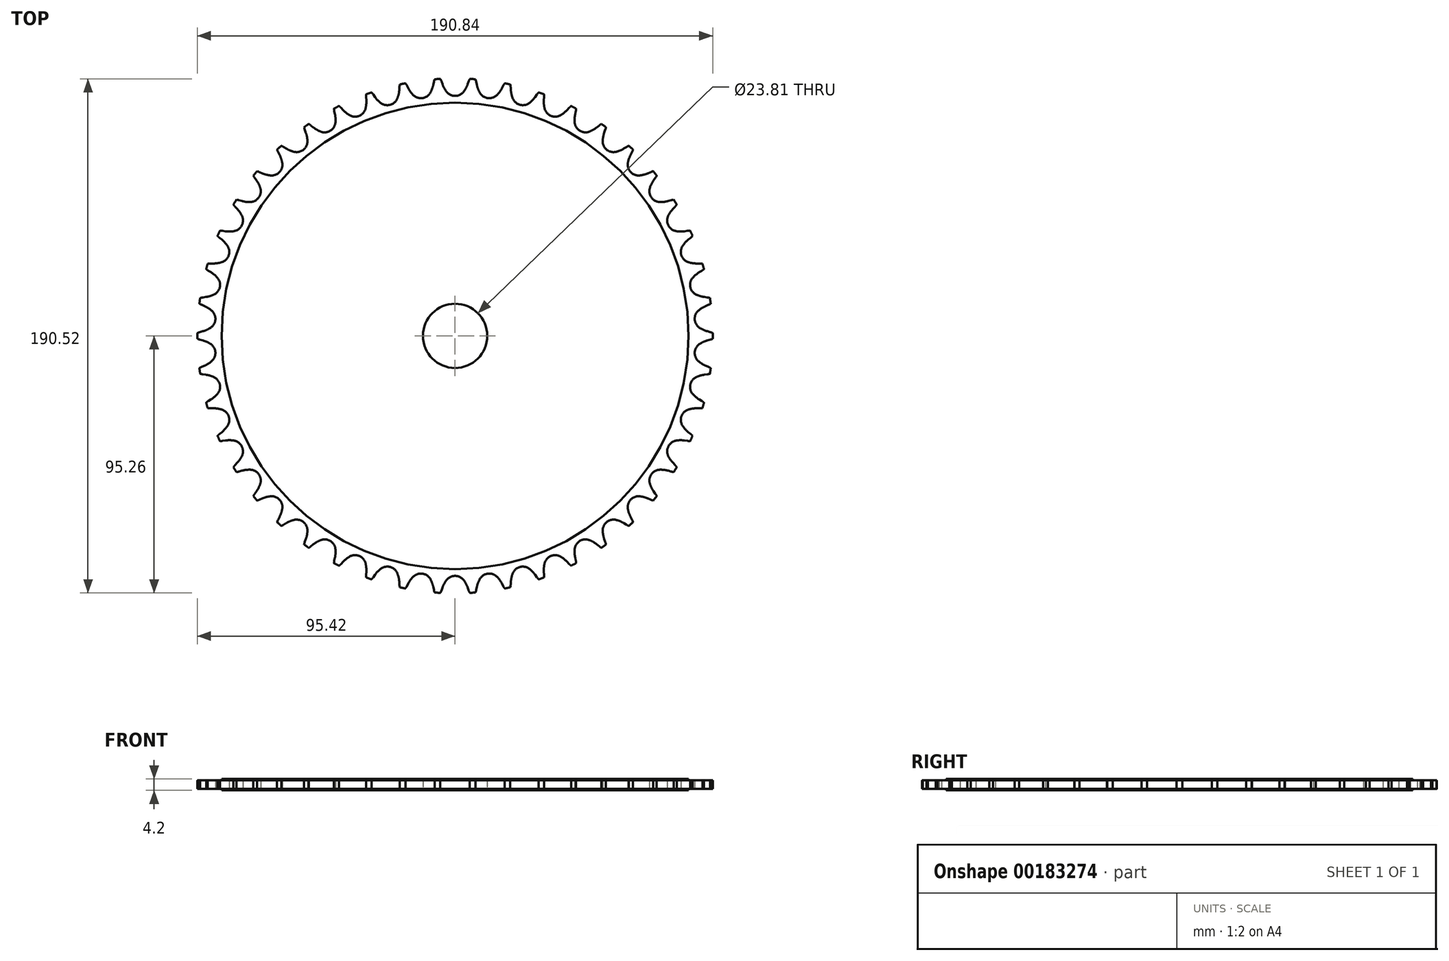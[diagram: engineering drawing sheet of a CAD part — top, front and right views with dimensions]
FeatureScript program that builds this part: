
annotation { "Feature Type Name" : "Feature", "Feature Type Description" : "" }
export const myFeature = defineFeature(function(context is Context, id is Id, definition is map)
    precondition{}
    {
        {
            var Q0;
            Q0=qCreatedBy(makeId("Top.planeOp"),FACE);
            var sketch = newSketch(context, id + "F0", { "sketchPlane" : qUnion([Q0])});
            skCircle(sketch, "E0", {"center": v(0, 0) * mm, "radius": 92.98 * mm, "construction": true});
            skArc(sketch, "E1", {"start": v(-3.24, 90.6) * mm, "mid": v(-1.81, 89.4) * mm, "end": v(0, 88.96) * mm});
            skArc(sketch, "E2", {"start": v(-4.67, 93.27) * mm, "mid": v(-4.05, 91.88) * mm, "end": v(-3.24, 90.6) * mm});
            skLineSegment(sketch, "E3", {"start": v(-4.67, 93.27) * mm, "end": v(-5.06, 94.36) * mm});
            skArc(sketch, "E4", {"start": v(-5.06, 94.36) * mm, "mid": v(-5.7, 95.68) * mm, "end": v(-6.62, 96.8) * mm});
            skArc(sketch, "E5.MirrorCS", {"start": v(3.24, 90.6) * mm, "mid": v(1.81, 89.4) * mm, "end": v(0, 88.96) * mm});
            skArc(sketch, "E6.MirrorCS", {"start": v(4.67, 93.27) * mm, "mid": v(4.05, 91.88) * mm, "end": v(3.24, 90.6) * mm});
            skLineSegment(sketch, "E7.MirrorCS", {"start": v(4.67, 93.27) * mm, "end": v(5.06, 94.36) * mm});
            skArc(sketch, "E8.MirrorCS", {"start": v(5.06, 94.36) * mm, "mid": v(5.7, 95.68) * mm, "end": v(6.62, 96.8) * mm});
            skArc(sketch, "E9.1.0", {"start": v(-17.86, 92.8) * mm, "mid": v(-18.67, 94) * mm, "end": v(-19.74, 95) * mm});
            skArc(sketch, "E9.1.1", {"start": v(-7.84, 94.17) * mm, "mid": v(-7.38, 95.56) * mm, "end": v(-6.62, 96.8) * mm});
            skArc(sketch, "E9.1.2", {"start": v(-9.13, 90.2) * mm, "mid": v(-10.38, 88.81) * mm, "end": v(-12.11, 88.13) * mm});
            skArc(sketch, "E9.1.3", {"start": v(-17.33, 91.77) * mm, "mid": v(-16.52, 90.48) * mm, "end": v(-15.54, 89.32) * mm});
            skArc(sketch, "E9.1.4", {"start": v(-15.54, 89.32) * mm, "mid": v(-13.97, 88.32) * mm, "end": v(-12.11, 88.13) * mm});
            skArc(sketch, "E9.1.5", {"start": v(-8.07, 93.04) * mm, "mid": v(-8.5, 91.58) * mm, "end": v(-9.13, 90.2) * mm});
            skLineSegment(sketch, "E9.1.6", {"start": v(-8.07, 93.04) * mm, "end": v(-7.84, 94.17) * mm});
            skLineSegment(sketch, "E9.1.7", {"start": v(-17.33, 91.77) * mm, "end": v(-17.86, 92.8) * mm});
            skArc(sketch, "E9.2.0", {"start": v(-30.33, 89.5) * mm, "mid": v(-31.3, 90.59) * mm, "end": v(-32.5, 91.43) * mm});
            skArc(sketch, "E9.2.1", {"start": v(-20.59, 92.23) * mm, "mid": v(-20.32, 93.67) * mm, "end": v(-19.74, 95) * mm});
            skArc(sketch, "E9.2.2", {"start": v(-21.33, 88.11) * mm, "mid": v(-22.37, 86.57) * mm, "end": v(-24, 85.66) * mm});
            skArc(sketch, "E9.2.3", {"start": v(-29.66, 88.55) * mm, "mid": v(-28.7, 87.38) * mm, "end": v(-27.56, 86.37) * mm});
            skArc(sketch, "E9.2.4", {"start": v(-27.56, 86.37) * mm, "mid": v(-25.86, 85.6) * mm, "end": v(-24, 85.66) * mm});
            skArc(sketch, "E9.2.5", {"start": v(-20.67, 91.07) * mm, "mid": v(-20.89, 89.57) * mm, "end": v(-21.33, 88.11) * mm});
            skLineSegment(sketch, "E9.2.6", {"start": v(-20.67, 91.07) * mm, "end": v(-20.59, 92.23) * mm});
            skLineSegment(sketch, "E9.2.7", {"start": v(-29.66, 88.55) * mm, "end": v(-30.33, 89.5) * mm});
            skArc(sketch, "E9.3.0", {"start": v(-42.23, 84.54) * mm, "mid": v(-43.34, 85.48) * mm, "end": v(-44.64, 86.16) * mm});
            skArc(sketch, "E9.3.1", {"start": v(-32.96, 88.57) * mm, "mid": v(-32.89, 90.03) * mm, "end": v(-32.5, 91.43) * mm});
            skArc(sketch, "E9.3.2", {"start": v(-33.13, 84.39) * mm, "mid": v(-33.95, 82.72) * mm, "end": v(-35.44, 81.6) * mm});
            skArc(sketch, "E9.3.3", {"start": v(-41.44, 83.69) * mm, "mid": v(-40.32, 82.66) * mm, "end": v(-39.06, 81.81) * mm});
            skArc(sketch, "E9.3.4", {"start": v(-39.06, 81.81) * mm, "mid": v(-37.28, 81.27) * mm, "end": v(-35.44, 81.6) * mm});
            skArc(sketch, "E9.3.5", {"start": v(-32.88, 87.4) * mm, "mid": v(-32.9, 85.9) * mm, "end": v(-33.13, 84.39) * mm});
            skLineSegment(sketch, "E9.3.6", {"start": v(-32.88, 87.4) * mm, "end": v(-32.96, 88.57) * mm});
            skLineSegment(sketch, "E9.3.7", {"start": v(-41.44, 83.69) * mm, "end": v(-42.23, 84.54) * mm});
            skArc(sketch, "E9.4.0", {"start": v(-53.35, 78) * mm, "mid": v(-54.58, 78.79) * mm, "end": v(-55.96, 79.27) * mm});
            skArc(sketch, "E9.4.1", {"start": v(-44.7, 83.25) * mm, "mid": v(-44.84, 84.7) * mm, "end": v(-44.64, 86.16) * mm});
            skArc(sketch, "E9.4.2", {"start": v(-44.31, 79.1) * mm, "mid": v(-44.9, 77.32) * mm, "end": v(-46.22, 76.01) * mm});
            skArc(sketch, "E9.4.3", {"start": v(-52.45, 77.27) * mm, "mid": v(-51.2, 76.4) * mm, "end": v(-49.84, 75.73) * mm});
            skArc(sketch, "E9.4.4", {"start": v(-49.84, 75.73) * mm, "mid": v(-48, 75.44) * mm, "end": v(-46.22, 76.01) * mm});
            skArc(sketch, "E9.4.5", {"start": v(-44.47, 82.12) * mm, "mid": v(-44.28, 80.61) * mm, "end": v(-44.31, 79.1) * mm});
            skLineSegment(sketch, "E9.4.6", {"start": v(-44.47, 82.12) * mm, "end": v(-44.7, 83.25) * mm});
            skLineSegment(sketch, "E9.4.7", {"start": v(-52.45, 77.27) * mm, "end": v(-53.35, 78) * mm});
            skArc(sketch, "E9.5.0", {"start": v(-63.47, 70) * mm, "mid": v(-64.8, 70.62) * mm, "end": v(-66.23, 70.92) * mm});
            skArc(sketch, "E9.5.1", {"start": v(-55.63, 76.39) * mm, "mid": v(-55.96, 77.81) * mm, "end": v(-55.96, 79.27) * mm});
            skArc(sketch, "E9.5.2", {"start": v(-54.67, 72.32) * mm, "mid": v(-55.01, 70.49) * mm, "end": v(-56.14, 69) * mm});
            skArc(sketch, "E9.5.3", {"start": v(-62.48, 69.4) * mm, "mid": v(-61.13, 68.72) * mm, "end": v(-59.69, 68.24) * mm});
            skArc(sketch, "E9.5.4", {"start": v(-59.69, 68.24) * mm, "mid": v(-57.82, 68.2) * mm, "end": v(-56.14, 69) * mm});
            skArc(sketch, "E9.5.5", {"start": v(-55.24, 75.3) * mm, "mid": v(-54.84, 73.83) * mm, "end": v(-54.67, 72.32) * mm});
            skLineSegment(sketch, "E9.5.6", {"start": v(-55.24, 75.3) * mm, "end": v(-55.63, 76.39) * mm});
            skLineSegment(sketch, "E9.5.7", {"start": v(-62.48, 69.4) * mm, "end": v(-63.47, 70) * mm});
            skArc(sketch, "E9.6.0", {"start": v(-72.42, 60.71) * mm, "mid": v(-73.81, 61.14) * mm, "end": v(-75.27, 61.24) * mm});
            skArc(sketch, "E9.6.1", {"start": v(-65.51, 68.1) * mm, "mid": v(-66.03, 69.47) * mm, "end": v(-66.23, 70.92) * mm});
            skArc(sketch, "E9.6.2", {"start": v(-64, 64.2) * mm, "mid": v(-64.1, 62.34) * mm, "end": v(-65.02, 60.72) * mm});
            skArc(sketch, "E9.6.3", {"start": v(-71.35, 60.25) * mm, "mid": v(-69.92, 59.75) * mm, "end": v(-68.42, 59.48) * mm});
            skArc(sketch, "E9.6.4", {"start": v(-68.42, 59.48) * mm, "mid": v(-66.57, 59.7) * mm, "end": v(-65.02, 60.72) * mm});
            skArc(sketch, "E9.6.5", {"start": v(-64.98, 67.08) * mm, "mid": v(-64.39, 65.68) * mm, "end": v(-64, 64.2) * mm});
            skLineSegment(sketch, "E9.6.6", {"start": v(-64.98, 67.08) * mm, "end": v(-65.51, 68.1) * mm});
            skLineSegment(sketch, "E9.6.7", {"start": v(-71.35, 60.25) * mm, "end": v(-72.42, 60.71) * mm});
            skArc(sketch, "E9.7.0", {"start": v(-80, 50.29) * mm, "mid": v(-81.45, 50.52) * mm, "end": v(-82.9, 50.42) * mm});
            skArc(sketch, "E9.7.1", {"start": v(-74.18, 58.55) * mm, "mid": v(-74.88, 59.83) * mm, "end": v(-75.27, 61.24) * mm});
            skArc(sketch, "E9.7.2", {"start": v(-72.15, 54.9) * mm, "mid": v(-71.99, 53.03) * mm, "end": v(-72.68, 51.3) * mm});
            skArc(sketch, "E9.7.3", {"start": v(-78.9, 49.97) * mm, "mid": v(-77.4, 49.68) * mm, "end": v(-75.88, 49.6) * mm});
            skArc(sketch, "E9.7.4", {"start": v(-75.88, 49.6) * mm, "mid": v(-74.08, 50.07) * mm, "end": v(-72.68, 51.3) * mm});
            skArc(sketch, "E9.7.5", {"start": v(-73.5, 57.6) * mm, "mid": v(-72.73, 56.3) * mm, "end": v(-72.15, 54.9) * mm});
            skLineSegment(sketch, "E9.7.6", {"start": v(-73.5, 57.6) * mm, "end": v(-74.18, 58.55) * mm});
            skLineSegment(sketch, "E9.7.7", {"start": v(-78.9, 49.97) * mm, "end": v(-80, 50.29) * mm});
            skArc(sketch, "E9.8.0", {"start": v(-86.1, 38.92) * mm, "mid": v(-87.57, 38.96) * mm, "end": v(-89, 38.66) * mm});
            skArc(sketch, "E9.8.1", {"start": v(-81.46, 47.9) * mm, "mid": v(-82.33, 49.08) * mm, "end": v(-82.9, 50.42) * mm});
            skArc(sketch, "E9.8.2", {"start": v(-78.95, 44.56) * mm, "mid": v(-78.54, 42.74) * mm, "end": v(-78.99, 40.93) * mm});
            skArc(sketch, "E9.8.3", {"start": v(-84.96, 38.76) * mm, "mid": v(-83.45, 38.68) * mm, "end": v(-81.93, 38.8) * mm});
            skArc(sketch, "E9.8.4", {"start": v(-81.93, 38.8) * mm, "mid": v(-80.2, 39.52) * mm, "end": v(-78.99, 40.93) * mm});
            skArc(sketch, "E9.8.5", {"start": v(-80.67, 47.06) * mm, "mid": v(-79.72, 45.87) * mm, "end": v(-78.95, 44.56) * mm});
            skLineSegment(sketch, "E9.8.6", {"start": v(-80.67, 47.06) * mm, "end": v(-81.46, 47.9) * mm});
            skLineSegment(sketch, "E9.8.7", {"start": v(-84.96, 38.76) * mm, "end": v(-86.1, 38.92) * mm});
            skArc(sketch, "E9.9.0", {"start": v(-90.6, 26.83) * mm, "mid": v(-92.06, 26.67) * mm, "end": v(-93.44, 26.18) * mm});
            skArc(sketch, "E9.9.1", {"start": v(-87.22, 36.37) * mm, "mid": v(-88.24, 37.41) * mm, "end": v(-89, 38.66) * mm});
            skArc(sketch, "E9.9.2", {"start": v(-84.29, 33.39) * mm, "mid": v(-83.63, 31.65) * mm, "end": v(-83.83, 29.8) * mm});
            skArc(sketch, "E9.9.3", {"start": v(-89.45, 26.83) * mm, "mid": v(-87.93, 26.95) * mm, "end": v(-86.45, 27.3) * mm});
            skArc(sketch, "E9.9.4", {"start": v(-86.45, 27.3) * mm, "mid": v(-84.84, 28.23) * mm, "end": v(-83.83, 29.8) * mm});
            skArc(sketch, "E9.9.5", {"start": v(-86.32, 35.64) * mm, "mid": v(-85.22, 34.59) * mm, "end": v(-84.29, 33.39) * mm});
            skLineSegment(sketch, "E9.9.6", {"start": v(-86.32, 35.64) * mm, "end": v(-87.22, 36.37) * mm});
            skLineSegment(sketch, "E9.9.7", {"start": v(-89.45, 26.83) * mm, "end": v(-90.6, 26.83) * mm});
            skArc(sketch, "E9.10.0", {"start": v(-93.42, 14.25) * mm, "mid": v(-94.83, 13.89) * mm, "end": v(-96.13, 13.21) * mm});
            skArc(sketch, "E9.10.1", {"start": v(-91.36, 24.15) * mm, "mid": v(-92.51, 25.05) * mm, "end": v(-93.44, 26.18) * mm});
            skArc(sketch, "E9.10.2", {"start": v(-88.05, 21.6) * mm, "mid": v(-87.16, 19.96) * mm, "end": v(-87.1, 18.1) * mm});
            skArc(sketch, "E9.10.3", {"start": v(-92.27, 14.4) * mm, "mid": v(-90.79, 14.73) * mm, "end": v(-89.36, 15.27) * mm});
            skArc(sketch, "E9.10.4", {"start": v(-89.36, 15.27) * mm, "mid": v(-87.9, 16.41) * mm, "end": v(-87.1, 18.1) * mm});
            skArc(sketch, "E9.10.5", {"start": v(-90.37, 23.55) * mm, "mid": v(-89.14, 22.66) * mm, "end": v(-88.05, 21.6) * mm});
            skLineSegment(sketch, "E9.10.6", {"start": v(-90.37, 23.55) * mm, "end": v(-91.36, 24.15) * mm});
            skLineSegment(sketch, "E9.10.7", {"start": v(-92.27, 14.4) * mm, "end": v(-93.42, 14.25) * mm});
            skArc(sketch, "E9.11.0", {"start": v(-94.49, 1.4) * mm, "mid": v(-95.84, 0.84) * mm, "end": v(-97.04, 0) * mm});
            skArc(sketch, "E9.11.1", {"start": v(-93.8, 11.49) * mm, "mid": v(-95.06, 12.22) * mm, "end": v(-96.13, 13.21) * mm});
            skArc(sketch, "E9.11.2", {"start": v(-90.17, 9.41) * mm, "mid": v(-89.06, 7.9) * mm, "end": v(-88.76, 6.07) * mm});
            skArc(sketch, "E9.11.3", {"start": v(-93.37, 1.7) * mm, "mid": v(-91.95, 2.23) * mm, "end": v(-90.61, 2.95) * mm});
            skArc(sketch, "E9.11.4", {"start": v(-90.61, 2.95) * mm, "mid": v(-89.31, 4.3) * mm, "end": v(-88.76, 6.07) * mm});
            skArc(sketch, "E9.11.5", {"start": v(-92.73, 11.02) * mm, "mid": v(-91.4, 10.31) * mm, "end": v(-90.17, 9.41) * mm});
            skLineSegment(sketch, "E9.11.6", {"start": v(-92.73, 11.02) * mm, "end": v(-93.8, 11.49) * mm});
            skLineSegment(sketch, "E9.11.7", {"start": v(-93.37, 1.7) * mm, "end": v(-94.49, 1.4) * mm});
            skArc(sketch, "E9.12.0", {"start": v(-93.8, -11.49) * mm, "mid": v(-95.06, -12.22) * mm, "end": v(-96.13, -13.21) * mm});
            skArc(sketch, "E9.12.1", {"start": v(-94.49, -1.4) * mm, "mid": v(-95.84, -0.84) * mm, "end": v(-97.04, 0) * mm});
            skArc(sketch, "E9.12.2", {"start": v(-90.61, -2.95) * mm, "mid": v(-89.31, -4.3) * mm, "end": v(-88.76, -6.07) * mm});
            skArc(sketch, "E9.12.3", {"start": v(-92.73, -11.02) * mm, "mid": v(-91.4, -10.31) * mm, "end": v(-90.17, -9.41) * mm});
            skArc(sketch, "E9.12.4", {"start": v(-90.17, -9.41) * mm, "mid": v(-89.06, -7.9) * mm, "end": v(-88.76, -6.07) * mm});
            skArc(sketch, "E9.12.5", {"start": v(-93.37, -1.7) * mm, "mid": v(-91.95, -2.23) * mm, "end": v(-90.61, -2.95) * mm});
            skLineSegment(sketch, "E9.12.6", {"start": v(-93.37, -1.7) * mm, "end": v(-94.49, -1.4) * mm});
            skLineSegment(sketch, "E9.12.7", {"start": v(-92.73, -11.02) * mm, "end": v(-93.8, -11.49) * mm});
            skArc(sketch, "E9.13.0", {"start": v(-91.36, -24.15) * mm, "mid": v(-92.51, -25.05) * mm, "end": v(-93.44, -26.18) * mm});
            skArc(sketch, "E9.13.1", {"start": v(-93.42, -14.25) * mm, "mid": v(-94.83, -13.89) * mm, "end": v(-96.13, -13.21) * mm});
            skArc(sketch, "E9.13.2", {"start": v(-89.36, -15.27) * mm, "mid": v(-87.9, -16.41) * mm, "end": v(-87.1, -18.1) * mm});
            skArc(sketch, "E9.13.3", {"start": v(-90.37, -23.55) * mm, "mid": v(-89.14, -22.66) * mm, "end": v(-88.05, -21.6) * mm});
            skArc(sketch, "E9.13.4", {"start": v(-88.05, -21.6) * mm, "mid": v(-87.16, -19.96) * mm, "end": v(-87.1, -18.1) * mm});
            skArc(sketch, "E9.13.5", {"start": v(-92.27, -14.4) * mm, "mid": v(-90.79, -14.73) * mm, "end": v(-89.36, -15.27) * mm});
            skLineSegment(sketch, "E9.13.6", {"start": v(-92.27, -14.4) * mm, "end": v(-93.42, -14.25) * mm});
            skLineSegment(sketch, "E9.13.7", {"start": v(-90.37, -23.55) * mm, "end": v(-91.36, -24.15) * mm});
            skArc(sketch, "E9.14.0", {"start": v(-87.22, -36.37) * mm, "mid": v(-88.24, -37.41) * mm, "end": v(-89, -38.66) * mm});
            skArc(sketch, "E9.14.1", {"start": v(-90.6, -26.83) * mm, "mid": v(-92.06, -26.67) * mm, "end": v(-93.44, -26.18) * mm});
            skArc(sketch, "E9.14.2", {"start": v(-86.45, -27.3) * mm, "mid": v(-84.84, -28.23) * mm, "end": v(-83.83, -29.8) * mm});
            skArc(sketch, "E9.14.3", {"start": v(-86.32, -35.64) * mm, "mid": v(-85.22, -34.59) * mm, "end": v(-84.29, -33.39) * mm});
            skArc(sketch, "E9.14.4", {"start": v(-84.29, -33.39) * mm, "mid": v(-83.63, -31.65) * mm, "end": v(-83.83, -29.8) * mm});
            skArc(sketch, "E9.14.5", {"start": v(-89.45, -26.83) * mm, "mid": v(-87.93, -26.95) * mm, "end": v(-86.45, -27.3) * mm});
            skLineSegment(sketch, "E9.14.6", {"start": v(-89.45, -26.83) * mm, "end": v(-90.6, -26.83) * mm});
            skLineSegment(sketch, "E9.14.7", {"start": v(-86.32, -35.64) * mm, "end": v(-87.22, -36.37) * mm});
            skArc(sketch, "E9.15.0", {"start": v(-81.46, -47.9) * mm, "mid": v(-82.33, -49.08) * mm, "end": v(-82.9, -50.42) * mm});
            skArc(sketch, "E9.15.1", {"start": v(-86.1, -38.92) * mm, "mid": v(-87.57, -38.96) * mm, "end": v(-89, -38.66) * mm});
            skArc(sketch, "E9.15.2", {"start": v(-81.93, -38.8) * mm, "mid": v(-80.2, -39.52) * mm, "end": v(-78.99, -40.93) * mm});
            skArc(sketch, "E9.15.3", {"start": v(-80.67, -47.06) * mm, "mid": v(-79.72, -45.87) * mm, "end": v(-78.95, -44.56) * mm});
            skArc(sketch, "E9.15.4", {"start": v(-78.95, -44.56) * mm, "mid": v(-78.54, -42.74) * mm, "end": v(-78.99, -40.93) * mm});
            skArc(sketch, "E9.15.5", {"start": v(-84.96, -38.76) * mm, "mid": v(-83.45, -38.68) * mm, "end": v(-81.93, -38.8) * mm});
            skLineSegment(sketch, "E9.15.6", {"start": v(-84.96, -38.76) * mm, "end": v(-86.1, -38.92) * mm});
            skLineSegment(sketch, "E9.15.7", {"start": v(-80.67, -47.06) * mm, "end": v(-81.46, -47.9) * mm});
            skArc(sketch, "E9.16.0", {"start": v(-74.18, -58.55) * mm, "mid": v(-74.88, -59.83) * mm, "end": v(-75.27, -61.24) * mm});
            skArc(sketch, "E9.16.1", {"start": v(-80, -50.29) * mm, "mid": v(-81.45, -50.52) * mm, "end": v(-82.9, -50.42) * mm});
            skArc(sketch, "E9.16.2", {"start": v(-75.88, -49.6) * mm, "mid": v(-74.08, -50.07) * mm, "end": v(-72.68, -51.3) * mm});
            skArc(sketch, "E9.16.3", {"start": v(-73.5, -57.6) * mm, "mid": v(-72.73, -56.3) * mm, "end": v(-72.15, -54.9) * mm});
            skArc(sketch, "E9.16.4", {"start": v(-72.15, -54.9) * mm, "mid": v(-71.99, -53.03) * mm, "end": v(-72.68, -51.3) * mm});
            skArc(sketch, "E9.16.5", {"start": v(-78.9, -49.97) * mm, "mid": v(-77.4, -49.68) * mm, "end": v(-75.88, -49.6) * mm});
            skLineSegment(sketch, "E9.16.6", {"start": v(-78.9, -49.97) * mm, "end": v(-80, -50.29) * mm});
            skLineSegment(sketch, "E9.16.7", {"start": v(-73.5, -57.6) * mm, "end": v(-74.18, -58.55) * mm});
            skArc(sketch, "E9.17.0", {"start": v(-65.51, -68.1) * mm, "mid": v(-66.03, -69.47) * mm, "end": v(-66.23, -70.92) * mm});
            skArc(sketch, "E9.17.1", {"start": v(-72.42, -60.71) * mm, "mid": v(-73.81, -61.14) * mm, "end": v(-75.27, -61.24) * mm});
            skArc(sketch, "E9.17.2", {"start": v(-68.42, -59.48) * mm, "mid": v(-66.57, -59.7) * mm, "end": v(-65.02, -60.72) * mm});
            skArc(sketch, "E9.17.3", {"start": v(-64.98, -67.08) * mm, "mid": v(-64.39, -65.68) * mm, "end": v(-64, -64.2) * mm});
            skArc(sketch, "E9.17.4", {"start": v(-64, -64.2) * mm, "mid": v(-64.1, -62.34) * mm, "end": v(-65.02, -60.72) * mm});
            skArc(sketch, "E9.17.5", {"start": v(-71.35, -60.25) * mm, "mid": v(-69.92, -59.75) * mm, "end": v(-68.42, -59.48) * mm});
            skLineSegment(sketch, "E9.17.6", {"start": v(-71.35, -60.25) * mm, "end": v(-72.42, -60.71) * mm});
            skLineSegment(sketch, "E9.17.7", {"start": v(-64.98, -67.08) * mm, "end": v(-65.51, -68.1) * mm});
            skArc(sketch, "E9.18.0", {"start": v(-55.63, -76.39) * mm, "mid": v(-55.96, -77.81) * mm, "end": v(-55.96, -79.27) * mm});
            skArc(sketch, "E9.18.1", {"start": v(-63.47, -70) * mm, "mid": v(-64.8, -70.62) * mm, "end": v(-66.23, -70.92) * mm});
            skArc(sketch, "E9.18.2", {"start": v(-59.69, -68.24) * mm, "mid": v(-57.82, -68.2) * mm, "end": v(-56.14, -69) * mm});
            skArc(sketch, "E9.18.3", {"start": v(-55.24, -75.3) * mm, "mid": v(-54.84, -73.83) * mm, "end": v(-54.67, -72.32) * mm});
            skArc(sketch, "E9.18.4", {"start": v(-54.67, -72.32) * mm, "mid": v(-55.01, -70.49) * mm, "end": v(-56.14, -69) * mm});
            skArc(sketch, "E9.18.5", {"start": v(-62.48, -69.4) * mm, "mid": v(-61.13, -68.72) * mm, "end": v(-59.69, -68.24) * mm});
            skLineSegment(sketch, "E9.18.6", {"start": v(-62.48, -69.4) * mm, "end": v(-63.47, -70) * mm});
            skLineSegment(sketch, "E9.18.7", {"start": v(-55.24, -75.3) * mm, "end": v(-55.63, -76.39) * mm});
            skArc(sketch, "E9.19.0", {"start": v(-44.7, -83.25) * mm, "mid": v(-44.84, -84.7) * mm, "end": v(-44.64, -86.16) * mm});
            skArc(sketch, "E9.19.1", {"start": v(-53.35, -78) * mm, "mid": v(-54.58, -78.79) * mm, "end": v(-55.96, -79.27) * mm});
            skArc(sketch, "E9.19.2", {"start": v(-49.84, -75.73) * mm, "mid": v(-48, -75.44) * mm, "end": v(-46.22, -76.01) * mm});
            skArc(sketch, "E9.19.3", {"start": v(-44.47, -82.12) * mm, "mid": v(-44.28, -80.61) * mm, "end": v(-44.31, -79.1) * mm});
            skArc(sketch, "E9.19.4", {"start": v(-44.31, -79.1) * mm, "mid": v(-44.9, -77.32) * mm, "end": v(-46.22, -76.01) * mm});
            skArc(sketch, "E9.19.5", {"start": v(-52.45, -77.27) * mm, "mid": v(-51.2, -76.4) * mm, "end": v(-49.84, -75.73) * mm});
            skLineSegment(sketch, "E9.19.6", {"start": v(-52.45, -77.27) * mm, "end": v(-53.35, -78) * mm});
            skLineSegment(sketch, "E9.19.7", {"start": v(-44.47, -82.12) * mm, "end": v(-44.7, -83.25) * mm});
            skArc(sketch, "E9.20.0", {"start": v(-32.96, -88.57) * mm, "mid": v(-32.89, -90.03) * mm, "end": v(-32.5, -91.43) * mm});
            skArc(sketch, "E9.20.1", {"start": v(-42.23, -84.54) * mm, "mid": v(-43.34, -85.48) * mm, "end": v(-44.64, -86.16) * mm});
            skArc(sketch, "E9.20.2", {"start": v(-39.06, -81.81) * mm, "mid": v(-37.28, -81.27) * mm, "end": v(-35.44, -81.6) * mm});
            skArc(sketch, "E9.20.3", {"start": v(-32.88, -87.4) * mm, "mid": v(-32.9, -85.9) * mm, "end": v(-33.13, -84.39) * mm});
            skArc(sketch, "E9.20.4", {"start": v(-33.13, -84.39) * mm, "mid": v(-33.95, -82.72) * mm, "end": v(-35.44, -81.6) * mm});
            skArc(sketch, "E9.20.5", {"start": v(-41.44, -83.69) * mm, "mid": v(-40.32, -82.66) * mm, "end": v(-39.06, -81.81) * mm});
            skLineSegment(sketch, "E9.20.6", {"start": v(-41.44, -83.69) * mm, "end": v(-42.23, -84.54) * mm});
            skLineSegment(sketch, "E9.20.7", {"start": v(-32.88, -87.4) * mm, "end": v(-32.96, -88.57) * mm});
            skArc(sketch, "E9.21.0", {"start": v(-20.59, -92.23) * mm, "mid": v(-20.32, -93.67) * mm, "end": v(-19.74, -95) * mm});
            skArc(sketch, "E9.21.1", {"start": v(-30.33, -89.5) * mm, "mid": v(-31.3, -90.59) * mm, "end": v(-32.5, -91.43) * mm});
            skArc(sketch, "E9.21.2", {"start": v(-27.56, -86.37) * mm, "mid": v(-25.86, -85.6) * mm, "end": v(-24, -85.66) * mm});
            skArc(sketch, "E9.21.3", {"start": v(-20.67, -91.07) * mm, "mid": v(-20.89, -89.57) * mm, "end": v(-21.33, -88.11) * mm});
            skArc(sketch, "E9.21.4", {"start": v(-21.33, -88.11) * mm, "mid": v(-22.37, -86.57) * mm, "end": v(-24, -85.66) * mm});
            skArc(sketch, "E9.21.5", {"start": v(-29.66, -88.55) * mm, "mid": v(-28.7, -87.38) * mm, "end": v(-27.56, -86.37) * mm});
            skLineSegment(sketch, "E9.21.6", {"start": v(-29.66, -88.55) * mm, "end": v(-30.33, -89.5) * mm});
            skLineSegment(sketch, "E9.21.7", {"start": v(-20.67, -91.07) * mm, "end": v(-20.59, -92.23) * mm});
            skArc(sketch, "E9.22.0", {"start": v(-7.84, -94.17) * mm, "mid": v(-7.38, -95.56) * mm, "end": v(-6.62, -96.8) * mm});
            skArc(sketch, "E9.22.1", {"start": v(-17.86, -92.8) * mm, "mid": v(-18.67, -94) * mm, "end": v(-19.74, -95) * mm});
            skArc(sketch, "E9.22.2", {"start": v(-15.54, -89.32) * mm, "mid": v(-13.97, -88.32) * mm, "end": v(-12.11, -88.13) * mm});
            skArc(sketch, "E9.22.3", {"start": v(-8.07, -93.04) * mm, "mid": v(-8.5, -91.58) * mm, "end": v(-9.13, -90.2) * mm});
            skArc(sketch, "E9.22.4", {"start": v(-9.13, -90.2) * mm, "mid": v(-10.38, -88.81) * mm, "end": v(-12.11, -88.13) * mm});
            skArc(sketch, "E9.22.5", {"start": v(-17.33, -91.77) * mm, "mid": v(-16.52, -90.48) * mm, "end": v(-15.54, -89.32) * mm});
            skLineSegment(sketch, "E9.22.6", {"start": v(-17.33, -91.77) * mm, "end": v(-17.86, -92.8) * mm});
            skLineSegment(sketch, "E9.22.7", {"start": v(-8.07, -93.04) * mm, "end": v(-7.84, -94.17) * mm});
            skArc(sketch, "E9.23.0", {"start": v(5.06, -94.36) * mm, "mid": v(5.7, -95.68) * mm, "end": v(6.62, -96.8) * mm});
            skArc(sketch, "E9.23.1", {"start": v(-5.06, -94.36) * mm, "mid": v(-5.7, -95.68) * mm, "end": v(-6.62, -96.8) * mm});
            skArc(sketch, "E9.23.2", {"start": v(-3.24, -90.6) * mm, "mid": v(-1.81, -89.4) * mm, "end": v(0, -88.96) * mm});
            skArc(sketch, "E9.23.3", {"start": v(4.67, -93.27) * mm, "mid": v(4.05, -91.88) * mm, "end": v(3.24, -90.6) * mm});
            skArc(sketch, "E9.23.4", {"start": v(3.24, -90.6) * mm, "mid": v(1.81, -89.4) * mm, "end": v(0, -88.96) * mm});
            skArc(sketch, "E9.23.5", {"start": v(-4.67, -93.27) * mm, "mid": v(-4.05, -91.88) * mm, "end": v(-3.24, -90.6) * mm});
            skLineSegment(sketch, "E9.23.6", {"start": v(-4.67, -93.27) * mm, "end": v(-5.06, -94.36) * mm});
            skLineSegment(sketch, "E9.23.7", {"start": v(4.67, -93.27) * mm, "end": v(5.06, -94.36) * mm});
            skArc(sketch, "E9.24.0", {"start": v(17.86, -92.8) * mm, "mid": v(18.67, -94) * mm, "end": v(19.74, -95) * mm});
            skArc(sketch, "E9.24.1", {"start": v(7.84, -94.17) * mm, "mid": v(7.38, -95.56) * mm, "end": v(6.62, -96.8) * mm});
            skArc(sketch, "E9.24.2", {"start": v(9.13, -90.2) * mm, "mid": v(10.38, -88.81) * mm, "end": v(12.11, -88.13) * mm});
            skArc(sketch, "E9.24.3", {"start": v(17.33, -91.77) * mm, "mid": v(16.52, -90.48) * mm, "end": v(15.54, -89.32) * mm});
            skArc(sketch, "E9.24.4", {"start": v(15.54, -89.32) * mm, "mid": v(13.97, -88.32) * mm, "end": v(12.11, -88.13) * mm});
            skArc(sketch, "E9.24.5", {"start": v(8.07, -93.04) * mm, "mid": v(8.5, -91.58) * mm, "end": v(9.13, -90.2) * mm});
            skLineSegment(sketch, "E9.24.6", {"start": v(8.07, -93.04) * mm, "end": v(7.84, -94.17) * mm});
            skLineSegment(sketch, "E9.24.7", {"start": v(17.33, -91.77) * mm, "end": v(17.86, -92.8) * mm});
            skArc(sketch, "E9.25.0", {"start": v(30.33, -89.5) * mm, "mid": v(31.3, -90.59) * mm, "end": v(32.5, -91.43) * mm});
            skArc(sketch, "E9.25.1", {"start": v(20.59, -92.23) * mm, "mid": v(20.32, -93.67) * mm, "end": v(19.74, -95) * mm});
            skArc(sketch, "E9.25.2", {"start": v(21.33, -88.11) * mm, "mid": v(22.37, -86.57) * mm, "end": v(24, -85.66) * mm});
            skArc(sketch, "E9.25.3", {"start": v(29.66, -88.55) * mm, "mid": v(28.7, -87.38) * mm, "end": v(27.56, -86.37) * mm});
            skArc(sketch, "E9.25.4", {"start": v(27.56, -86.37) * mm, "mid": v(25.86, -85.6) * mm, "end": v(24, -85.66) * mm});
            skArc(sketch, "E9.25.5", {"start": v(20.67, -91.07) * mm, "mid": v(20.89, -89.57) * mm, "end": v(21.33, -88.11) * mm});
            skLineSegment(sketch, "E9.25.6", {"start": v(20.67, -91.07) * mm, "end": v(20.59, -92.23) * mm});
            skLineSegment(sketch, "E9.25.7", {"start": v(29.66, -88.55) * mm, "end": v(30.33, -89.5) * mm});
            skArc(sketch, "E9.26.0", {"start": v(42.23, -84.54) * mm, "mid": v(43.34, -85.48) * mm, "end": v(44.64, -86.16) * mm});
            skArc(sketch, "E9.26.1", {"start": v(32.96, -88.57) * mm, "mid": v(32.89, -90.03) * mm, "end": v(32.5, -91.43) * mm});
            skArc(sketch, "E9.26.2", {"start": v(33.13, -84.39) * mm, "mid": v(33.95, -82.72) * mm, "end": v(35.44, -81.6) * mm});
            skArc(sketch, "E9.26.3", {"start": v(41.44, -83.69) * mm, "mid": v(40.32, -82.66) * mm, "end": v(39.06, -81.81) * mm});
            skArc(sketch, "E9.26.4", {"start": v(39.06, -81.81) * mm, "mid": v(37.28, -81.27) * mm, "end": v(35.44, -81.6) * mm});
            skArc(sketch, "E9.26.5", {"start": v(32.88, -87.4) * mm, "mid": v(32.9, -85.9) * mm, "end": v(33.13, -84.39) * mm});
            skLineSegment(sketch, "E9.26.6", {"start": v(32.88, -87.4) * mm, "end": v(32.96, -88.57) * mm});
            skLineSegment(sketch, "E9.26.7", {"start": v(41.44, -83.69) * mm, "end": v(42.23, -84.54) * mm});
            skArc(sketch, "E9.27.0", {"start": v(53.35, -78) * mm, "mid": v(54.58, -78.79) * mm, "end": v(55.96, -79.27) * mm});
            skArc(sketch, "E9.27.1", {"start": v(44.7, -83.25) * mm, "mid": v(44.84, -84.7) * mm, "end": v(44.64, -86.16) * mm});
            skArc(sketch, "E9.27.2", {"start": v(44.31, -79.1) * mm, "mid": v(44.9, -77.32) * mm, "end": v(46.22, -76.01) * mm});
            skArc(sketch, "E9.27.3", {"start": v(52.45, -77.27) * mm, "mid": v(51.2, -76.4) * mm, "end": v(49.84, -75.73) * mm});
            skArc(sketch, "E9.27.4", {"start": v(49.84, -75.73) * mm, "mid": v(48, -75.44) * mm, "end": v(46.22, -76.01) * mm});
            skArc(sketch, "E9.27.5", {"start": v(44.47, -82.12) * mm, "mid": v(44.28, -80.61) * mm, "end": v(44.31, -79.1) * mm});
            skLineSegment(sketch, "E9.27.6", {"start": v(44.47, -82.12) * mm, "end": v(44.7, -83.25) * mm});
            skLineSegment(sketch, "E9.27.7", {"start": v(52.45, -77.27) * mm, "end": v(53.35, -78) * mm});
            skArc(sketch, "E9.28.0", {"start": v(63.47, -70) * mm, "mid": v(64.8, -70.62) * mm, "end": v(66.23, -70.92) * mm});
            skArc(sketch, "E9.28.1", {"start": v(55.63, -76.39) * mm, "mid": v(55.96, -77.81) * mm, "end": v(55.96, -79.27) * mm});
            skArc(sketch, "E9.28.2", {"start": v(54.67, -72.32) * mm, "mid": v(55.01, -70.49) * mm, "end": v(56.14, -69) * mm});
            skArc(sketch, "E9.28.3", {"start": v(62.48, -69.4) * mm, "mid": v(61.13, -68.72) * mm, "end": v(59.69, -68.24) * mm});
            skArc(sketch, "E9.28.4", {"start": v(59.69, -68.24) * mm, "mid": v(57.82, -68.2) * mm, "end": v(56.14, -69) * mm});
            skArc(sketch, "E9.28.5", {"start": v(55.24, -75.3) * mm, "mid": v(54.84, -73.83) * mm, "end": v(54.67, -72.32) * mm});
            skLineSegment(sketch, "E9.28.6", {"start": v(55.24, -75.3) * mm, "end": v(55.63, -76.39) * mm});
            skLineSegment(sketch, "E9.28.7", {"start": v(62.48, -69.4) * mm, "end": v(63.47, -70) * mm});
            skArc(sketch, "E9.29.0", {"start": v(72.42, -60.71) * mm, "mid": v(73.81, -61.14) * mm, "end": v(75.27, -61.24) * mm});
            skArc(sketch, "E9.29.1", {"start": v(65.51, -68.1) * mm, "mid": v(66.03, -69.47) * mm, "end": v(66.23, -70.92) * mm});
            skArc(sketch, "E9.29.2", {"start": v(64, -64.2) * mm, "mid": v(64.1, -62.34) * mm, "end": v(65.02, -60.72) * mm});
            skArc(sketch, "E9.29.3", {"start": v(71.35, -60.25) * mm, "mid": v(69.92, -59.75) * mm, "end": v(68.42, -59.48) * mm});
            skArc(sketch, "E9.29.4", {"start": v(68.42, -59.48) * mm, "mid": v(66.57, -59.7) * mm, "end": v(65.02, -60.72) * mm});
            skArc(sketch, "E9.29.5", {"start": v(64.98, -67.08) * mm, "mid": v(64.39, -65.68) * mm, "end": v(64, -64.2) * mm});
            skLineSegment(sketch, "E9.29.6", {"start": v(64.98, -67.08) * mm, "end": v(65.51, -68.1) * mm});
            skLineSegment(sketch, "E9.29.7", {"start": v(71.35, -60.25) * mm, "end": v(72.42, -60.71) * mm});
            skArc(sketch, "E9.30.0", {"start": v(80, -50.29) * mm, "mid": v(81.45, -50.52) * mm, "end": v(82.9, -50.42) * mm});
            skArc(sketch, "E9.30.1", {"start": v(74.18, -58.55) * mm, "mid": v(74.88, -59.83) * mm, "end": v(75.27, -61.24) * mm});
            skArc(sketch, "E9.30.2", {"start": v(72.15, -54.9) * mm, "mid": v(71.99, -53.03) * mm, "end": v(72.68, -51.3) * mm});
            skArc(sketch, "E9.30.3", {"start": v(78.9, -49.97) * mm, "mid": v(77.4, -49.68) * mm, "end": v(75.88, -49.6) * mm});
            skArc(sketch, "E9.30.4", {"start": v(75.88, -49.6) * mm, "mid": v(74.08, -50.07) * mm, "end": v(72.68, -51.3) * mm});
            skArc(sketch, "E9.30.5", {"start": v(73.5, -57.6) * mm, "mid": v(72.73, -56.3) * mm, "end": v(72.15, -54.9) * mm});
            skLineSegment(sketch, "E9.30.6", {"start": v(73.5, -57.6) * mm, "end": v(74.18, -58.55) * mm});
            skLineSegment(sketch, "E9.30.7", {"start": v(78.9, -49.97) * mm, "end": v(80, -50.29) * mm});
            skArc(sketch, "E9.31.0", {"start": v(86.1, -38.92) * mm, "mid": v(87.57, -38.96) * mm, "end": v(89, -38.66) * mm});
            skArc(sketch, "E9.31.1", {"start": v(81.46, -47.9) * mm, "mid": v(82.33, -49.08) * mm, "end": v(82.9, -50.42) * mm});
            skArc(sketch, "E9.31.2", {"start": v(78.95, -44.56) * mm, "mid": v(78.54, -42.74) * mm, "end": v(78.99, -40.93) * mm});
            skArc(sketch, "E9.31.3", {"start": v(84.96, -38.76) * mm, "mid": v(83.45, -38.68) * mm, "end": v(81.93, -38.8) * mm});
            skArc(sketch, "E9.31.4", {"start": v(81.93, -38.8) * mm, "mid": v(80.2, -39.52) * mm, "end": v(78.99, -40.93) * mm});
            skArc(sketch, "E9.31.5", {"start": v(80.67, -47.06) * mm, "mid": v(79.72, -45.87) * mm, "end": v(78.95, -44.56) * mm});
            skLineSegment(sketch, "E9.31.6", {"start": v(80.67, -47.06) * mm, "end": v(81.46, -47.9) * mm});
            skLineSegment(sketch, "E9.31.7", {"start": v(84.96, -38.76) * mm, "end": v(86.1, -38.92) * mm});
            skArc(sketch, "E9.32.0", {"start": v(90.6, -26.83) * mm, "mid": v(92.06, -26.67) * mm, "end": v(93.44, -26.18) * mm});
            skArc(sketch, "E9.32.1", {"start": v(87.22, -36.37) * mm, "mid": v(88.24, -37.41) * mm, "end": v(89, -38.66) * mm});
            skArc(sketch, "E9.32.2", {"start": v(84.29, -33.39) * mm, "mid": v(83.63, -31.65) * mm, "end": v(83.83, -29.8) * mm});
            skArc(sketch, "E9.32.3", {"start": v(89.45, -26.83) * mm, "mid": v(87.93, -26.95) * mm, "end": v(86.45, -27.3) * mm});
            skArc(sketch, "E9.32.4", {"start": v(86.45, -27.3) * mm, "mid": v(84.84, -28.23) * mm, "end": v(83.83, -29.8) * mm});
            skArc(sketch, "E9.32.5", {"start": v(86.32, -35.64) * mm, "mid": v(85.22, -34.59) * mm, "end": v(84.29, -33.39) * mm});
            skLineSegment(sketch, "E9.32.6", {"start": v(86.32, -35.64) * mm, "end": v(87.22, -36.37) * mm});
            skLineSegment(sketch, "E9.32.7", {"start": v(89.45, -26.83) * mm, "end": v(90.6, -26.83) * mm});
            skArc(sketch, "E9.33.0", {"start": v(93.42, -14.25) * mm, "mid": v(94.83, -13.89) * mm, "end": v(96.13, -13.21) * mm});
            skArc(sketch, "E9.33.1", {"start": v(91.36, -24.15) * mm, "mid": v(92.51, -25.05) * mm, "end": v(93.44, -26.18) * mm});
            skArc(sketch, "E9.33.2", {"start": v(88.05, -21.6) * mm, "mid": v(87.16, -19.96) * mm, "end": v(87.1, -18.1) * mm});
            skArc(sketch, "E9.33.3", {"start": v(92.27, -14.4) * mm, "mid": v(90.79, -14.73) * mm, "end": v(89.36, -15.27) * mm});
            skArc(sketch, "E9.33.4", {"start": v(89.36, -15.27) * mm, "mid": v(87.9, -16.41) * mm, "end": v(87.1, -18.1) * mm});
            skArc(sketch, "E9.33.5", {"start": v(90.37, -23.55) * mm, "mid": v(89.14, -22.66) * mm, "end": v(88.05, -21.6) * mm});
            skLineSegment(sketch, "E9.33.6", {"start": v(90.37, -23.55) * mm, "end": v(91.36, -24.15) * mm});
            skLineSegment(sketch, "E9.33.7", {"start": v(92.27, -14.4) * mm, "end": v(93.42, -14.25) * mm});
            skArc(sketch, "E9.34.0", {"start": v(94.49, -1.4) * mm, "mid": v(95.84, -0.84) * mm, "end": v(97.04, 0) * mm});
            skArc(sketch, "E9.34.1", {"start": v(93.8, -11.49) * mm, "mid": v(95.06, -12.22) * mm, "end": v(96.13, -13.21) * mm});
            skArc(sketch, "E9.34.2", {"start": v(90.17, -9.41) * mm, "mid": v(89.06, -7.9) * mm, "end": v(88.76, -6.07) * mm});
            skArc(sketch, "E9.34.3", {"start": v(93.37, -1.7) * mm, "mid": v(91.95, -2.23) * mm, "end": v(90.61, -2.95) * mm});
            skArc(sketch, "E9.34.4", {"start": v(90.61, -2.95) * mm, "mid": v(89.31, -4.3) * mm, "end": v(88.76, -6.07) * mm});
            skArc(sketch, "E9.34.5", {"start": v(92.73, -11.02) * mm, "mid": v(91.4, -10.31) * mm, "end": v(90.17, -9.41) * mm});
            skLineSegment(sketch, "E9.34.6", {"start": v(92.73, -11.02) * mm, "end": v(93.8, -11.49) * mm});
            skLineSegment(sketch, "E9.34.7", {"start": v(93.37, -1.7) * mm, "end": v(94.49, -1.4) * mm});
            skArc(sketch, "E9.35.0", {"start": v(93.8, 11.49) * mm, "mid": v(95.06, 12.22) * mm, "end": v(96.13, 13.21) * mm});
            skArc(sketch, "E9.35.1", {"start": v(94.49, 1.4) * mm, "mid": v(95.84, 0.84) * mm, "end": v(97.04, 0) * mm});
            skArc(sketch, "E9.35.2", {"start": v(90.61, 2.95) * mm, "mid": v(89.31, 4.3) * mm, "end": v(88.76, 6.07) * mm});
            skArc(sketch, "E9.35.3", {"start": v(92.73, 11.02) * mm, "mid": v(91.4, 10.31) * mm, "end": v(90.17, 9.41) * mm});
            skArc(sketch, "E9.35.4", {"start": v(90.17, 9.41) * mm, "mid": v(89.06, 7.9) * mm, "end": v(88.76, 6.07) * mm});
            skArc(sketch, "E9.35.5", {"start": v(93.37, 1.7) * mm, "mid": v(91.95, 2.23) * mm, "end": v(90.61, 2.95) * mm});
            skLineSegment(sketch, "E9.35.6", {"start": v(93.37, 1.7) * mm, "end": v(94.49, 1.4) * mm});
            skLineSegment(sketch, "E9.35.7", {"start": v(92.73, 11.02) * mm, "end": v(93.8, 11.49) * mm});
            skArc(sketch, "E9.36.0", {"start": v(91.36, 24.15) * mm, "mid": v(92.51, 25.05) * mm, "end": v(93.44, 26.18) * mm});
            skArc(sketch, "E9.36.1", {"start": v(93.42, 14.25) * mm, "mid": v(94.83, 13.89) * mm, "end": v(96.13, 13.21) * mm});
            skArc(sketch, "E9.36.2", {"start": v(89.36, 15.27) * mm, "mid": v(87.9, 16.41) * mm, "end": v(87.1, 18.1) * mm});
            skArc(sketch, "E9.36.3", {"start": v(90.37, 23.55) * mm, "mid": v(89.14, 22.66) * mm, "end": v(88.05, 21.6) * mm});
            skArc(sketch, "E9.36.4", {"start": v(88.05, 21.6) * mm, "mid": v(87.16, 19.96) * mm, "end": v(87.1, 18.1) * mm});
            skArc(sketch, "E9.36.5", {"start": v(92.27, 14.4) * mm, "mid": v(90.79, 14.73) * mm, "end": v(89.36, 15.27) * mm});
            skLineSegment(sketch, "E9.36.6", {"start": v(92.27, 14.4) * mm, "end": v(93.42, 14.25) * mm});
            skLineSegment(sketch, "E9.36.7", {"start": v(90.37, 23.55) * mm, "end": v(91.36, 24.15) * mm});
            skArc(sketch, "E9.37.0", {"start": v(87.22, 36.37) * mm, "mid": v(88.24, 37.41) * mm, "end": v(89, 38.66) * mm});
            skArc(sketch, "E9.37.1", {"start": v(90.6, 26.83) * mm, "mid": v(92.06, 26.67) * mm, "end": v(93.44, 26.18) * mm});
            skArc(sketch, "E9.37.2", {"start": v(86.45, 27.3) * mm, "mid": v(84.84, 28.23) * mm, "end": v(83.83, 29.8) * mm});
            skArc(sketch, "E9.37.3", {"start": v(86.32, 35.64) * mm, "mid": v(85.22, 34.59) * mm, "end": v(84.29, 33.39) * mm});
            skArc(sketch, "E9.37.4", {"start": v(84.29, 33.39) * mm, "mid": v(83.63, 31.65) * mm, "end": v(83.83, 29.8) * mm});
            skArc(sketch, "E9.37.5", {"start": v(89.45, 26.83) * mm, "mid": v(87.93, 26.95) * mm, "end": v(86.45, 27.3) * mm});
            skLineSegment(sketch, "E9.37.6", {"start": v(89.45, 26.83) * mm, "end": v(90.6, 26.83) * mm});
            skLineSegment(sketch, "E9.37.7", {"start": v(86.32, 35.64) * mm, "end": v(87.22, 36.37) * mm});
            skArc(sketch, "E9.38.0", {"start": v(81.46, 47.9) * mm, "mid": v(82.33, 49.08) * mm, "end": v(82.9, 50.42) * mm});
            skArc(sketch, "E9.38.1", {"start": v(86.1, 38.92) * mm, "mid": v(87.57, 38.96) * mm, "end": v(89, 38.66) * mm});
            skArc(sketch, "E9.38.2", {"start": v(81.93, 38.8) * mm, "mid": v(80.2, 39.52) * mm, "end": v(78.99, 40.93) * mm});
            skArc(sketch, "E9.38.3", {"start": v(80.67, 47.06) * mm, "mid": v(79.72, 45.87) * mm, "end": v(78.95, 44.56) * mm});
            skArc(sketch, "E9.38.4", {"start": v(78.95, 44.56) * mm, "mid": v(78.54, 42.74) * mm, "end": v(78.99, 40.93) * mm});
            skArc(sketch, "E9.38.5", {"start": v(84.96, 38.76) * mm, "mid": v(83.45, 38.68) * mm, "end": v(81.93, 38.8) * mm});
            skLineSegment(sketch, "E9.38.6", {"start": v(84.96, 38.76) * mm, "end": v(86.1, 38.92) * mm});
            skLineSegment(sketch, "E9.38.7", {"start": v(80.67, 47.06) * mm, "end": v(81.46, 47.9) * mm});
            skArc(sketch, "E9.39.0", {"start": v(74.18, 58.55) * mm, "mid": v(74.88, 59.83) * mm, "end": v(75.27, 61.24) * mm});
            skArc(sketch, "E9.39.1", {"start": v(80, 50.29) * mm, "mid": v(81.45, 50.52) * mm, "end": v(82.9, 50.42) * mm});
            skArc(sketch, "E9.39.2", {"start": v(75.88, 49.6) * mm, "mid": v(74.08, 50.07) * mm, "end": v(72.68, 51.3) * mm});
            skArc(sketch, "E9.39.3", {"start": v(73.5, 57.6) * mm, "mid": v(72.73, 56.3) * mm, "end": v(72.15, 54.9) * mm});
            skArc(sketch, "E9.39.4", {"start": v(72.15, 54.9) * mm, "mid": v(71.99, 53.03) * mm, "end": v(72.68, 51.3) * mm});
            skArc(sketch, "E9.39.5", {"start": v(78.9, 49.97) * mm, "mid": v(77.4, 49.68) * mm, "end": v(75.88, 49.6) * mm});
            skLineSegment(sketch, "E9.39.6", {"start": v(78.9, 49.97) * mm, "end": v(80, 50.29) * mm});
            skLineSegment(sketch, "E9.39.7", {"start": v(73.5, 57.6) * mm, "end": v(74.18, 58.55) * mm});
            skArc(sketch, "E9.40.0", {"start": v(65.51, 68.1) * mm, "mid": v(66.03, 69.47) * mm, "end": v(66.23, 70.92) * mm});
            skArc(sketch, "E9.40.1", {"start": v(72.42, 60.71) * mm, "mid": v(73.81, 61.14) * mm, "end": v(75.27, 61.24) * mm});
            skArc(sketch, "E9.40.2", {"start": v(68.42, 59.48) * mm, "mid": v(66.57, 59.7) * mm, "end": v(65.02, 60.72) * mm});
            skArc(sketch, "E9.40.3", {"start": v(64.98, 67.08) * mm, "mid": v(64.39, 65.68) * mm, "end": v(64, 64.2) * mm});
            skArc(sketch, "E9.40.4", {"start": v(64, 64.2) * mm, "mid": v(64.1, 62.34) * mm, "end": v(65.02, 60.72) * mm});
            skArc(sketch, "E9.40.5", {"start": v(71.35, 60.25) * mm, "mid": v(69.92, 59.75) * mm, "end": v(68.42, 59.48) * mm});
            skLineSegment(sketch, "E9.40.6", {"start": v(71.35, 60.25) * mm, "end": v(72.42, 60.71) * mm});
            skLineSegment(sketch, "E9.40.7", {"start": v(64.98, 67.08) * mm, "end": v(65.51, 68.1) * mm});
            skArc(sketch, "E9.41.0", {"start": v(55.63, 76.39) * mm, "mid": v(55.96, 77.81) * mm, "end": v(55.96, 79.27) * mm});
            skArc(sketch, "E9.41.1", {"start": v(63.47, 70) * mm, "mid": v(64.8, 70.62) * mm, "end": v(66.23, 70.92) * mm});
            skArc(sketch, "E9.41.2", {"start": v(59.69, 68.24) * mm, "mid": v(57.82, 68.2) * mm, "end": v(56.14, 69) * mm});
            skArc(sketch, "E9.41.3", {"start": v(55.24, 75.3) * mm, "mid": v(54.84, 73.83) * mm, "end": v(54.67, 72.32) * mm});
            skArc(sketch, "E9.41.4", {"start": v(54.67, 72.32) * mm, "mid": v(55.01, 70.49) * mm, "end": v(56.14, 69) * mm});
            skArc(sketch, "E9.41.5", {"start": v(62.48, 69.4) * mm, "mid": v(61.13, 68.72) * mm, "end": v(59.69, 68.24) * mm});
            skLineSegment(sketch, "E9.41.6", {"start": v(62.48, 69.4) * mm, "end": v(63.47, 70) * mm});
            skLineSegment(sketch, "E9.41.7", {"start": v(55.24, 75.3) * mm, "end": v(55.63, 76.39) * mm});
            skArc(sketch, "E9.42.0", {"start": v(44.7, 83.25) * mm, "mid": v(44.84, 84.7) * mm, "end": v(44.64, 86.16) * mm});
            skArc(sketch, "E9.42.1", {"start": v(53.35, 78) * mm, "mid": v(54.58, 78.79) * mm, "end": v(55.96, 79.27) * mm});
            skArc(sketch, "E9.42.2", {"start": v(49.84, 75.73) * mm, "mid": v(48, 75.44) * mm, "end": v(46.22, 76.01) * mm});
            skArc(sketch, "E9.42.3", {"start": v(44.47, 82.12) * mm, "mid": v(44.28, 80.61) * mm, "end": v(44.31, 79.1) * mm});
            skArc(sketch, "E9.42.4", {"start": v(44.31, 79.1) * mm, "mid": v(44.9, 77.32) * mm, "end": v(46.22, 76.01) * mm});
            skArc(sketch, "E9.42.5", {"start": v(52.45, 77.27) * mm, "mid": v(51.2, 76.4) * mm, "end": v(49.84, 75.73) * mm});
            skLineSegment(sketch, "E9.42.6", {"start": v(52.45, 77.27) * mm, "end": v(53.35, 78) * mm});
            skLineSegment(sketch, "E9.42.7", {"start": v(44.47, 82.12) * mm, "end": v(44.7, 83.25) * mm});
            skArc(sketch, "E9.43.0", {"start": v(32.96, 88.57) * mm, "mid": v(32.89, 90.03) * mm, "end": v(32.5, 91.43) * mm});
            skArc(sketch, "E9.43.1", {"start": v(42.23, 84.54) * mm, "mid": v(43.34, 85.48) * mm, "end": v(44.64, 86.16) * mm});
            skArc(sketch, "E9.43.2", {"start": v(39.06, 81.81) * mm, "mid": v(37.28, 81.27) * mm, "end": v(35.44, 81.6) * mm});
            skArc(sketch, "E9.43.3", {"start": v(32.88, 87.4) * mm, "mid": v(32.9, 85.9) * mm, "end": v(33.13, 84.39) * mm});
            skArc(sketch, "E9.43.4", {"start": v(33.13, 84.39) * mm, "mid": v(33.95, 82.72) * mm, "end": v(35.44, 81.6) * mm});
            skArc(sketch, "E9.43.5", {"start": v(41.44, 83.69) * mm, "mid": v(40.32, 82.66) * mm, "end": v(39.06, 81.81) * mm});
            skLineSegment(sketch, "E9.43.6", {"start": v(41.44, 83.69) * mm, "end": v(42.23, 84.54) * mm});
            skLineSegment(sketch, "E9.43.7", {"start": v(32.88, 87.4) * mm, "end": v(32.96, 88.57) * mm});
            skArc(sketch, "E9.44.0", {"start": v(20.59, 92.23) * mm, "mid": v(20.32, 93.67) * mm, "end": v(19.74, 95) * mm});
            skArc(sketch, "E9.44.1", {"start": v(30.33, 89.5) * mm, "mid": v(31.3, 90.59) * mm, "end": v(32.5, 91.43) * mm});
            skArc(sketch, "E9.44.2", {"start": v(27.56, 86.37) * mm, "mid": v(25.86, 85.6) * mm, "end": v(24, 85.66) * mm});
            skArc(sketch, "E9.44.3", {"start": v(20.67, 91.07) * mm, "mid": v(20.89, 89.57) * mm, "end": v(21.33, 88.11) * mm});
            skArc(sketch, "E9.44.4", {"start": v(21.33, 88.11) * mm, "mid": v(22.37, 86.57) * mm, "end": v(24, 85.66) * mm});
            skArc(sketch, "E9.44.5", {"start": v(29.66, 88.55) * mm, "mid": v(28.7, 87.38) * mm, "end": v(27.56, 86.37) * mm});
            skLineSegment(sketch, "E9.44.6", {"start": v(29.66, 88.55) * mm, "end": v(30.33, 89.5) * mm});
            skLineSegment(sketch, "E9.44.7", {"start": v(20.67, 91.07) * mm, "end": v(20.59, 92.23) * mm});
            skArc(sketch, "E9.45.0", {"start": v(7.84, 94.17) * mm, "mid": v(7.38, 95.56) * mm, "end": v(6.62, 96.8) * mm});
            skArc(sketch, "E9.45.1", {"start": v(17.86, 92.8) * mm, "mid": v(18.67, 94) * mm, "end": v(19.74, 95) * mm});
            skArc(sketch, "E9.45.2", {"start": v(15.54, 89.32) * mm, "mid": v(13.97, 88.32) * mm, "end": v(12.11, 88.13) * mm});
            skArc(sketch, "E9.45.3", {"start": v(8.07, 93.04) * mm, "mid": v(8.5, 91.58) * mm, "end": v(9.13, 90.2) * mm});
            skArc(sketch, "E9.45.4", {"start": v(9.13, 90.2) * mm, "mid": v(10.38, 88.81) * mm, "end": v(12.11, 88.13) * mm});
            skArc(sketch, "E9.45.5", {"start": v(17.33, 91.77) * mm, "mid": v(16.52, 90.48) * mm, "end": v(15.54, 89.32) * mm});
            skLineSegment(sketch, "E9.45.6", {"start": v(17.33, 91.77) * mm, "end": v(17.86, 92.8) * mm});
            skLineSegment(sketch, "E9.45.7", {"start": v(8.07, 93.04) * mm, "end": v(7.84, 94.17) * mm});
            skCircle(sketch, "E10", {"center": v(0, 0) * mm, "radius": 95.42 * mm});
            skCircle(sketch, "E11", {"center": v(0, 0) * mm, "radius": 86.46 * mm});
            skCircle(sketch, "E12", {"center": v(0, 0) * mm, "radius": 11.9 * mm});
            skSolve(sketch);
        }
        {
            var Q0;
            Q0=makeQuery(id+"F0.imprint","IMPRINT",FACE,{"disambiguationData":[TD([[makeQuery(id+"F0.imprint","IMPRINT",EDGE,{"derivedFrom":sQuery(id+"F0.wireOp",EDGE,"E11")}),1.0]])]});
            extrude(context, id + "F1", {"entities" : qUnion([Q0]), "endBound" : BoundingType.SYMMETRIC, "depth" : 4.2 * mm});
        }
        {
            var Q0;
            Q0=makeQuery(id+"F0.imprint","IMPRINT",FACE,{"disambiguationData":[TD([[makeQuery(id+"F0.imprint","IMPRINT",EDGE,{"derivedFrom":sQuery(id+"F0.wireOp",EDGE,"E1")}),-1.0]])]});
            extrude(context, id + "F2", {"entities" : qUnion([Q0]), "operationType" : NewBodyOperationType.ADD, "endBound" : BoundingType.SYMMETRIC, "depth" : 3.18 * mm});
        }
    });
